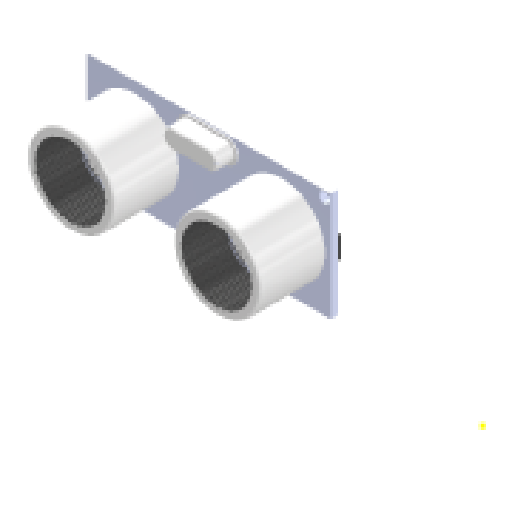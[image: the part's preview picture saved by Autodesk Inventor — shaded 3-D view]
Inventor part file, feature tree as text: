
AUTODESK INVENTOR PART (.ipt)
format: ipt  version: 2025 (Build 290162000, 162)  size: 2,167,808 bytes
history: native  units: in
note: dims shown in document units (in); Inventor stores cm internally (conversion verified against a paired STEP export)
features: sketch x2, other x2, extrude x1, mirror x1
ambient origin geometry x8: Origin, YZ Plane, XZ Plane, XY Plane, X Axis, Y Axis, Z Axis, Center Point
bodies: Solid1 (feature_tree), Solid2 (feature_tree), Solid3 (feature_tree)
feature tree (6):
  extrude  "Extrusion1"  [1 undecoded]
  sketch  "Sketch2"
  sketch  "Sketch1"  dims[d0=1.1063in d1=0.0in]
  other  "Boss-Extrude14"
  mirror  "Mirror11[2]"
  other  "Cut-Extrude4"
note: 1 required parameter value undecoded (feature->parameter linkage not recoverable at this tier; creation-order binding heuristic only, values carry confidence <= 0.55)
